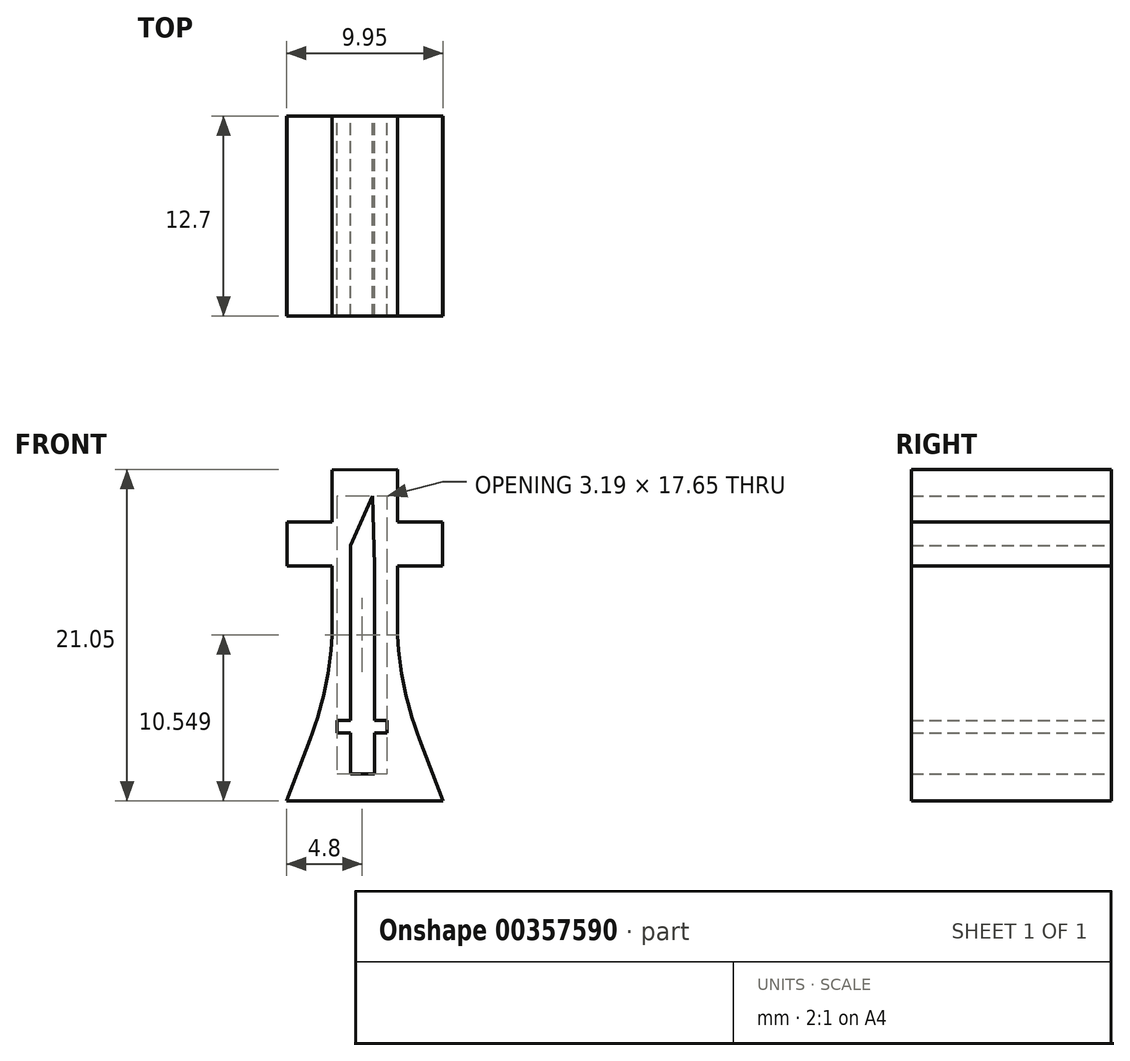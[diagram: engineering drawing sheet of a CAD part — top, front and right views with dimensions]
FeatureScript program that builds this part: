
annotation { "Feature Type Name" : "Feature", "Feature Type Description" : "" }
export const myFeature = defineFeature(function(context is Context, id is Id, definition is map)
    precondition{}
    {
        {
            var Q0;
            Q0=qCreatedBy(makeId("Front.planeOp"),FACE);
            var sketch = newSketch(context, id + "F0", { "sketchPlane" : qUnion([Q0])});
            skLineSegment(sketch, "E0", {"start": v(-24.29, 7.37) * mm, "end": v(-24.29, 10.14) * mm});
            skLineSegment(sketch, "E1", {"start": v(-24.33, -7.56) * mm, "end": v(-14.38, -7.56) * mm});
            skLineSegment(sketch, "E2", {"start": v(-21.42, 3.93) * mm, "end": v(-21.42, 7.37) * mm});
            skLineSegment(sketch, "E3", {"start": v(-17.3, 3.93) * mm, "end": v(-17.3, 7.37) * mm});
            skLineSegment(sketch, "E4", {"start": v(-21.42, 10.14) * mm, "end": v(-21.42, 13.46) * mm});
            skLineSegment(sketch, "E5", {"start": v(-17.3, 10.14) * mm, "end": v(-17.3, 13.5) * mm});
            skLineSegment(sketch, "E6", {"start": v(-21.42, 13.46) * mm, "end": v(-17.3, 13.5) * mm});
            skLineSegment(sketch, "E7", {"start": v(-14.43, 10.14) * mm, "end": v(-14.43, 7.37) * mm});
            skLineSegment(sketch, "E8", {"start": v(-24.29, 10.14) * mm, "end": v(-21.42, 10.14) * mm});
            skLineSegment(sketch, "E9", {"start": v(-17.3, 10.14) * mm, "end": v(-14.43, 10.14) * mm});
            skLineSegment(sketch, "E10", {"start": v(-24.29, 7.37) * mm, "end": v(-21.42, 7.37) * mm});
            skLineSegment(sketch, "E11", {"start": v(-14.43, 7.37) * mm, "end": v(-17.3, 7.37) * mm});
            skLineSegment(sketch, "E12", {"start": v(-24.33, -7.56) * mm, "end": v(-22.84, -3.67) * mm});
            skLineSegment(sketch, "E13", {"start": v(-14.38, -7.56) * mm, "end": v(-15.88, -3.67) * mm});
            skPoint(sketch, "E14.endSnap0", {"position": v(-17.3, 11.82) * mm});
            skLineSegment(sketch, "E15", {"start": v(-20.27, 0) * mm, "end": v(-20.27, 7.37) * mm});
            skLineSegment(sketch, "E16", {"start": v(-18.72, 0) * mm, "end": v(-18.72, 7.37) * mm});
            skLineSegment(sketch, "E17", {"start": v(-20.27, 7.37) * mm, "end": v(-20.27, 8.66) * mm});
            skLineSegment(sketch, "E18", {"start": v(-18.88, 11.82) * mm, "end": v(-18.72, 7.37) * mm});
            skLineSegment(sketch, "E19", {"start": v(-20.27, 8.66) * mm, "end": v(-18.88, 11.82) * mm});
            skLineSegment(sketch, "E20", {"start": v(-20.27, 0) * mm, "end": v(-20.27, -2.45) * mm});
            skLineSegment(sketch, "E21", {"start": v(-20.27, -2.45) * mm, "end": v(-21.13, -2.45) * mm});
            skLineSegment(sketch, "E22", {"start": v(-21.13, -2.45) * mm, "end": v(-21.13, -3.23) * mm});
            skLineSegment(sketch, "E23", {"start": v(-21.13, -3.23) * mm, "end": v(-20.27, -3.23) * mm});
            skLineSegment(sketch, "E24", {"start": v(-20.27, -3.23) * mm, "end": v(-20.27, -5.84) * mm});
            skLineSegment(sketch, "E25", {"start": v(-20.27, -5.84) * mm, "end": v(-18.72, -5.84) * mm});
            skLineSegment(sketch, "E26", {"start": v(-18.72, -5.84) * mm, "end": v(-18.72, -3.23) * mm});
            skLineSegment(sketch, "E27", {"start": v(-18.72, -3.23) * mm, "end": v(-17.93, -3.23) * mm});
            skLineSegment(sketch, "E28", {"start": v(-17.93, -3.23) * mm, "end": v(-17.93, -2.45) * mm});
            skLineSegment(sketch, "E29", {"start": v(-17.93, -2.45) * mm, "end": v(-18.72, -2.45) * mm});
            skLineSegment(sketch, "E30", {"start": v(-18.72, -2.45) * mm, "end": v(-18.72, 0) * mm});
            skPoint(sketch, "E31.visualSharp", {"position": v(-21.42, 0) * mm});
            skArc(sketch, "E31.filletArc", {"start": v(-22.84, -3.67) * mm, "mid": v(-21.78, 0.07) * mm, "end": v(-21.42, 3.93) * mm});
            skPoint(sketch, "E32.visualSharp", {"position": v(-17.3, 0) * mm});
            skArc(sketch, "E32.filletArc", {"start": v(-17.3, 3.93) * mm, "mid": v(-16.93, 0.07) * mm, "end": v(-15.88, -3.67) * mm});
            skSolve(sketch);
        }
        {
            var Q0;
            Q0=makeQuery(id+"F0.imprint","IMPRINT",FACE,{"disambiguationData":[TD([[makeQuery(id+"F0.imprint","IMPRINT",EDGE,{"derivedFrom":sQuery(id+"F0.wireOp",EDGE,"E0")}),-1.0]])]});
            extrude(context, id + "F1", {"entities" : qUnion([Q0]), "depth" : 12.7 * mm});
        }
    });
